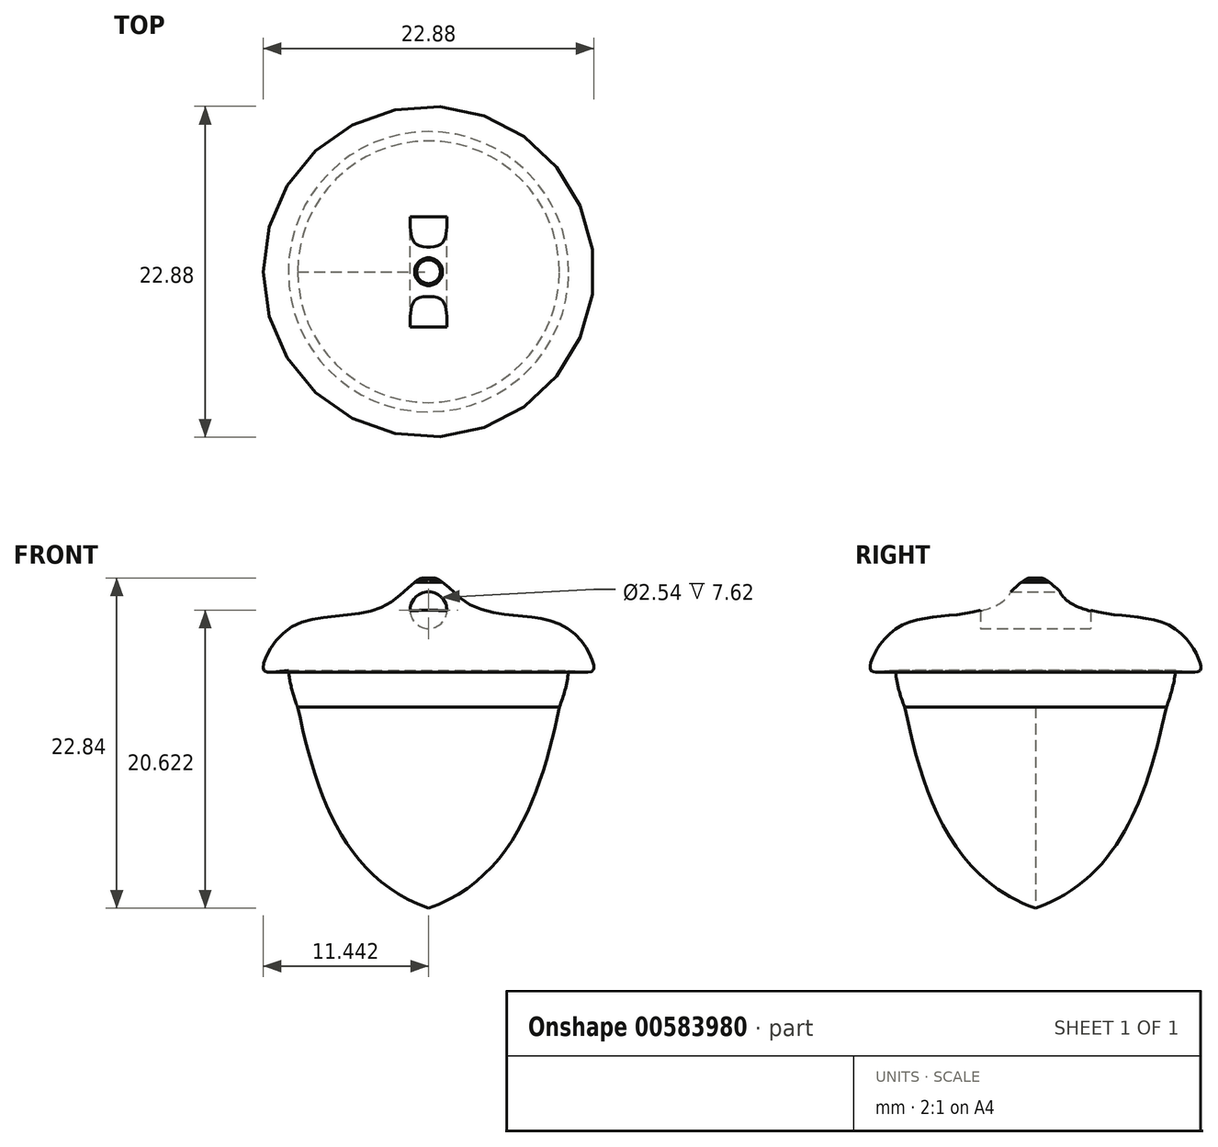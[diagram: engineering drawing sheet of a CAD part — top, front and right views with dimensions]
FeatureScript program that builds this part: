
annotation { "Feature Type Name" : "Feature", "Feature Type Description" : "" }
export const myFeature = defineFeature(function(context is Context, id is Id, definition is map)
    precondition{}
    {
        {
            var Q0;
            Q0=qCreatedBy(makeId("Front.planeOp"),FACE);
            var sketch = newSketch(context, id + "F0", { "sketchPlane" : qUnion([Q0])});
            skArc(sketch, "E0", {"start": v(-71.73, 37.7) * mm, "mid": v(-71.58, 36.15) * mm, "end": v(-71.14, 34.66) * mm});
            skLineSegment(sketch, "E1", {"start": v(-63.6, 37.7) * mm, "end": v(-63.6, 29.58) * mm});
            skLineSegment(sketch, "E2", {"start": v(-63.6, 29.58) * mm, "end": v(-63.6, 23.06) * mm});
            skLineSegment(sketch, "E3", {"start": v(-63.6, 37.7) * mm, "end": v(-71.73, 37.7) * mm});
            skFitSpline(sketch, "E4", {"points": [v(-71.73, 37.7) * mm, v(-63.6, 23.06) * mm, v(51.1, 67.8) * mm], "startDerivative": vector(13.09, -69.95) * mm, "endDerivative": vector(203.33, 103.48) * mm});
            skLineSegment(sketch, "E5", {"start": v(-63.6, 37.7) * mm, "end": v(-63.6, 6.45) * mm});
            skPoint(sketch, "E5.endSnap0", {"position": v(-63.6, 33.64) * mm});
            skLineSegment(sketch, "E6", {"start": v(-63.6, 37.7) * mm, "end": v(-63.6, 51.2) * mm});
            skSolve(sketch);
        }
        {
            var Q0;
            Q0 = qSketchRegion(id + "F0", true);
            var Q1;
            Q1=sQuery(id+"F0.wireOp",EDGE,"E5");
            revolve(context, id + "F1", {"entities" : qUnion([Q0]), "axis" : qUnion([Q1]), "revolveType" : RevolveType.FULL});
        }
        {
            var Q0;
            Q0=qCreatedBy(makeId("Front.planeOp"),FACE);
            var sketch = newSketch(context, id + "F2", { "sketchPlane" : qUnion([Q0])});
            skFitSpline(sketch, "E7", {"points": [v(-72.8, 36.67) * mm, v(-73.13, 36.9) * mm, v(-71.42, 39.3) * mm, v(-65.95, 40.58) * mm, v(-63.6, 41.94) * mm, v(-63.6, 30.18) * mm, v(-68.6, 35.94) * mm, v(-72.8, 36.67) * mm]});
            skLineSegment(sketch, "E8", {"start": v(-63.6, 42.44) * mm, "end": v(-64.28, 41.94) * mm});
            skPoint(sketch, "E9.0", {"position": v(-63.6, 23.06) * mm});
            skLineSegment(sketch, "E10", {"start": v(-63.6, 23.06) * mm, "end": v(-63.6, 29.27) * mm});
            skLineSegment(sketch, "E11", {"start": v(-64.4, 41.86) * mm, "end": v(-64.28, 41.94) * mm});
            skLineSegment(sketch, "E12", {"start": v(-63.6, 42.44) * mm, "end": v(-63.6, 41.94) * mm});
            skLineSegment(sketch, "E13", {"start": v(-63.6, 41.94) * mm, "end": v(-63.6, 30.18) * mm});
            skSolve(sketch);
        }
        {
            var Q0;
            Q0=makeQuery(id+"F2.imprint","IMPRINT",FACE,{"disambiguationData":[TD([[makeQuery(id+"F2.imprint","IMPRINT",EDGE,{"derivedFrom":sQuery(id+"F2.wireOp",EDGE,"E7")}),-1.0]])]});
            var Q1;
            Q1=sQuery(id+"F2.wireOp",EDGE,"E10");
            revolve(context, id + "F3", {"operationType" : NewBodyOperationType.ADD, "entities" : qUnion([Q0]), "axis" : qUnion([Q1]), "revolveType" : RevolveType.FULL});
        }
        {
            var Q0;
            Q0=makeQuery(id+"F1.opRevolve","SWEPT_BODY",BODY,{"disambiguationData":[OSD([sQuery(id+"F0.wireOp",EDGE,"E0"),sQuery(id+"F0.wireOp",EDGE,"E3"),sQuery(id+"F0.wireOp",EDGE,"E4"),sQuery(id+"F0.wireOp",EDGE,"E5")])]});
            var Q1;
            Q1=makeQuery(id+"F3.opRevolve","SWEPT_VERTEX",VERTEX,{"disambiguationData":[OSD([sQuery(id+"F2.wireOp",EDGE,"E8"),sQuery(id+"F2.wireOp",EDGE,"E12")])]});
            transform(context, id + "F4", {"entities" : qUnion([Q0]), "transformType" : TransformType.SCALE_UNIFORMLY, "scale" : 1.2, "scalePoint" : qUnion([Q1]), "makeCopy" : false});
        }
        {
            var Q0;
            Q0=qCreatedBy(makeId("Front.planeOp"),FACE);
            var sketch = newSketch(context, id + "F5", { "sketchPlane" : qUnion([Q0])});
            skPoint(sketch, "E14.0", {"position": v(-63.6, 42.44) * mm});
            skLineSegment(sketch, "E15", {"start": v(-63.6, 42.44) * mm, "end": v(-63.6, 39.9) * mm});
            skCircle(sketch, "E16", {"center": v(-63.6, 39.9) * mm, "radius": 1.27 * mm});
            skSolve(sketch);
        }
        {
            var Q0;
            Q0 = qSketchRegion(id + "F5", true);
            extrude(context, id + "F6", {"entities" : qUnion([Q0]), "operationType" : NewBodyOperationType.REMOVE, "endBound" : BoundingType.SYMMETRIC, "depth" : 7.62 * mm, "offsetDistance" : 25.4 * mm});
        }
    });
